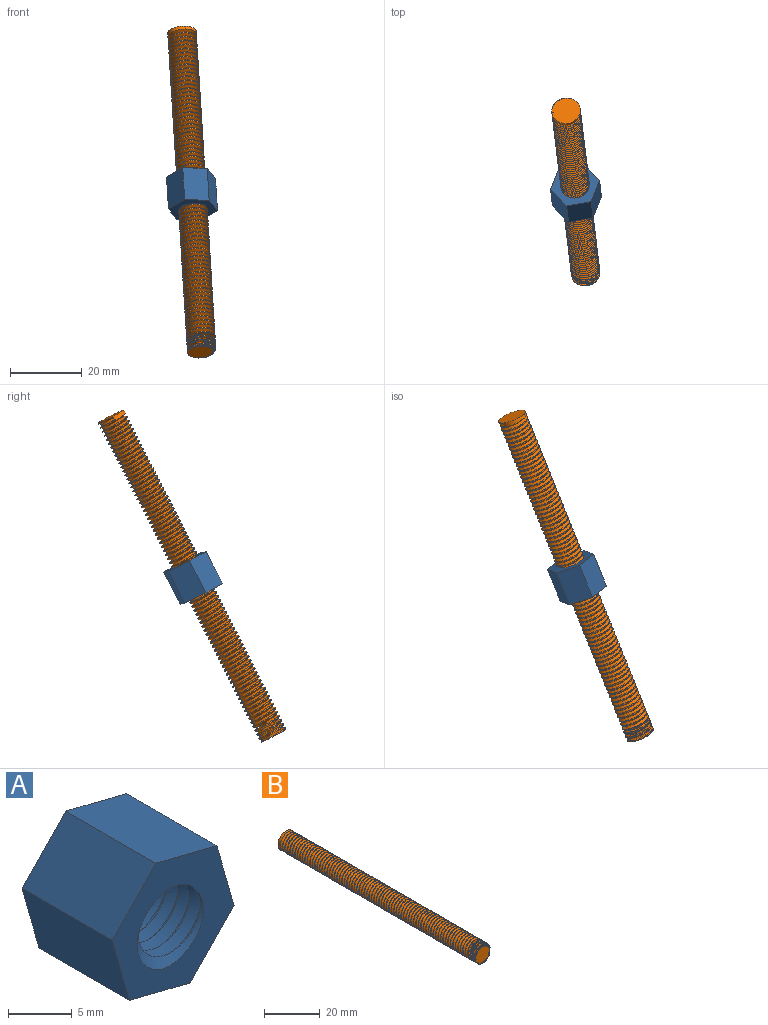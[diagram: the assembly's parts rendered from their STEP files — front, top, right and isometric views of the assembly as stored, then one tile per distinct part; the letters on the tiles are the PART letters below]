
ASSEMBLY  parts=2 mates=1
PART A: 11 faces, bbox 14x11.9x13.9 mm
  f0: plane 14.04x13.93mm, normal (0,-1,0), area 83.7mm2, adj f2,f3,f4,f5,f6,f7,f8,f9
  f1: plane 14.04x13.93mm, normal (0,1,0), area 83.7mm2, adj f2,f3,f4,f5,f6,f7,f8,f9
  f2: plane 10x5mm, normal (-0.72,0,0.7), area 69.6mm2, adj f0,f1,f3,f7
  f3: plane 10x6.69mm, normal (-0.96,0,-0.27), area 69.6mm2, adj f0,f1,f2,f4
  f4: plane 10x6.75mm, normal (-0.24,0,-0.97), area 69.6mm2, adj f0,f1,f3,f5
  f5: plane 10x5mm, normal (0.72,0,-0.7), area 69.6mm2, adj f0,f1,f4,f6
  f6: plane 10x6.69mm, normal (0.96,0,0.27), area 69.6mm2, adj f0,f1,f5,f7
  f7: plane 10x6.75mm, normal (0.24,0,0.97), area 69.6mm2, adj f0,f1,f2,f6
  f8: cylinder r=4mm len=10mm, axis (0,1,0), area 49.6mm2, adj f0,f1,f9,f10
  f9: bspline ~11.33x9.24mm, area 180.1mm2, adj f0,f1,f8,f10
  f10: bspline ~11.13x9.24mm, area 179.2mm2, adj f0,f1,f8,f9
PART B: 6 faces, bbox 8.5x101.1x9.8 mm
  f0: cylinder r=4mm len=100mm, axis (0,1,0), area 1230.1mm2, adj f1,f2,f3,f4,f5
  f1: plane 7.93x7.91mm, normal (0,-1,0), area 42.2mm2, adj f0,f4,f5
  f2: plane 8x8mm, normal (0,1,0), area 50.3mm2, adj f0
  f3: plane 1x0.87mm, normal (0,0,-1), area 0.4mm2, adj f0,f4,f5
  f4: bspline ~100.5x9.24mm, area 1792mm2, adj f0,f1,f3,f5
  f5: bspline ~100.08x9.24mm, area 1782.5mm2, adj f0,f1,f3,f4
PLACE A rot(axis=(0.29,0.81,0.51),125deg) t=(-28.18,-31.66,-12)mm
PLACE B rot(axis=(0.99,0.06,0.1),63.2deg) t=(-28.21,-31.41,-11.51)mm
MATE cylindrical B.f0 <-> A.f8  axis (0.05,-0.45,-0.89) through (-25.47,-54.05,-56.01)mm
